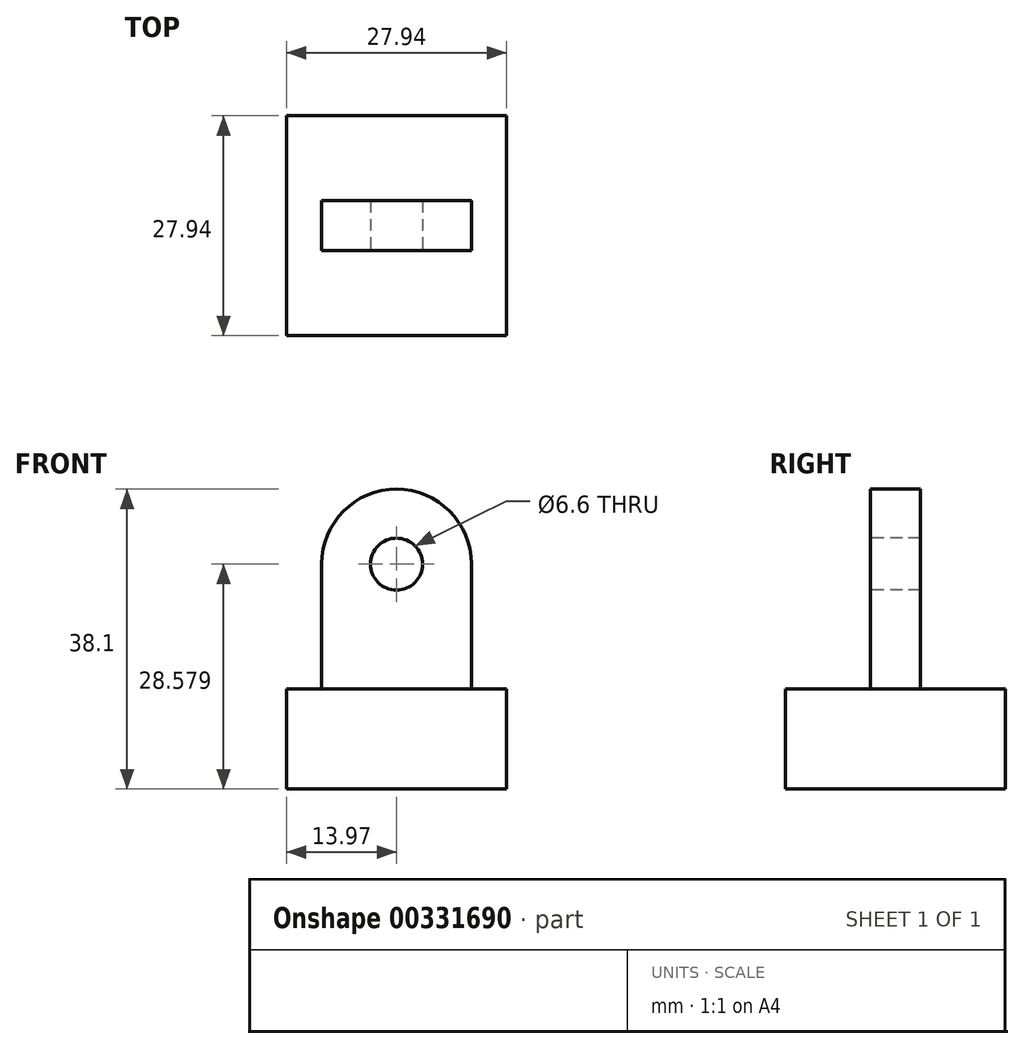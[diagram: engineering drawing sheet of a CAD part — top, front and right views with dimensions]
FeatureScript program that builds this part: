
annotation { "Feature Type Name" : "Feature", "Feature Type Description" : "" }
export const myFeature = defineFeature(function(context is Context, id is Id, definition is map)
    precondition{}
    {
        {
            var Q0;
            Q0=qCreatedBy(makeId("Front.planeOp"),FACE);
            var sketch = newSketch(context, id + "F0", { "sketchPlane" : qUnion([Q0])});
            skLineSegment(sketch, "E0.bottom", {"start": v(-27.94, -193.09) * mm, "end": v(0, -193.09) * mm});
            skLineSegment(sketch, "E0.top", {"start": v(-27.94, -205.79) * mm, "end": v(0, -205.79) * mm});
            skLineSegment(sketch, "E0.left", {"start": v(-27.94, -193.09) * mm, "end": v(-27.94, -205.79) * mm});
            skLineSegment(sketch, "E0.right", {"start": v(0, -193.09) * mm, "end": v(0, -205.79) * mm});
            skSolve(sketch);
        }
        {
            var Q0;
            Q0=makeQuery(id+"F0.imprint","IMPRINT",FACE,{"disambiguationData":[TD([[makeQuery(id+"F0.imprint","IMPRINT",EDGE,{"derivedFrom":sQuery(id+"F0.wireOp",EDGE,"E0.bottom")}),-1.0]])]});
            extrude(context, id + "F1", {"entities" : qUnion([Q0]), "oppositeDirection" : true, "depth" : 27.94 * mm});
        }
        {
            var Q0;
            Q0=makeQuery(id+"F1.opExtrude","SWEPT_FACE",FACE,{"disambiguationData":[OSD([sQuery(id+"F0.wireOp",EDGE,"E0.bottom")])]});
            var sketch = newSketch(context, id + "F2", { "sketchPlane" : qUnion([Q0])});
            skLineSegment(sketch, "E1.bottom", {"start": v(-23.5, 17.15) * mm, "end": v(-4.44, 17.15) * mm});
            skLineSegment(sketch, "E1.top", {"start": v(-23.5, 10.8) * mm, "end": v(-4.44, 10.8) * mm});
            skLineSegment(sketch, "E1.left", {"start": v(-23.5, 17.15) * mm, "end": v(-23.5, 10.8) * mm});
            skLineSegment(sketch, "E1.right", {"start": v(-4.44, 17.15) * mm, "end": v(-4.44, 10.8) * mm});
            skSolve(sketch);
        }
        {
            var Q0;
            Q0=makeQuery(id+"F2.imprint","IMPRINT",FACE,{"disambiguationData":[TD([[makeQuery(id+"F2.imprint","IMPRINT",EDGE,{"derivedFrom":sQuery(id+"F2.wireOp",EDGE,"E1.bottom")}),-1.0]])]});
            extrude(context, id + "F3", {"entities" : qUnion([Q0]), "operationType" : NewBodyOperationType.ADD, "depth" : 25.4 * mm});
        }
        {
            var Q0;
            Q0=makeQuery(id+"F3.opExtrude","CAP_EDGE",EDGE,{"disambiguationData":[OSD([sQuery(id+"F2.wireOp",EDGE,"E1.right")])],"isStart":false});
            var Q1;
            Q1=makeQuery(id+"F3.opExtrude","CAP_EDGE",EDGE,{"disambiguationData":[OSD([sQuery(id+"F2.wireOp",EDGE,"E1.left")])],"isStart":false});
            fillet(context, id + "F4", {"entities" : qUnion([Q0, Q1]), "radius" : 9.52 * mm, "tangentPropagation" : true, "allowEdgeOverflow" : false});
        }
        {
            var Q0;
            Q0=makeQuery(id+"F3.opExtrude","SWEPT_FACE",FACE,{"disambiguationData":[OSD([sQuery(id+"F2.wireOp",EDGE,"E1.top")])]});
            var sketch = newSketch(context, id + "F5", { "sketchPlane" : qUnion([Q0])});
            skCircle(sketch, "E2", {"center": v(-13.97, -177.21) * mm, "radius": 3.3 * mm});
            skSolve(sketch);
        }
        {
            var Q0;
            Q0=qSketchRegion(id+"F5",true);
            extrude(context, id + "F6", {"entities" : qUnion([Q0]), "operationType" : NewBodyOperationType.REMOVE, "oppositeDirection" : true, "depth" : 6.35 * mm});
        }
        {
            var Q0;
            Q0=makeQuery(id+"F1.opExtrude","SWEPT_FACE",FACE,{"disambiguationData":[OSD([sQuery(id+"F0.wireOp",EDGE,"E0.left")])]});
            var sketch = newSketch(context, id + "F7", { "sketchPlane" : qUnion([Q0])});
            skLineSegment(sketch, "E3.bottom", {"start": v(-26.35, -170.86) * mm, "end": v(-24.77, -170.86) * mm});
            skLineSegment(sketch, "E3.top", {"start": v(-26.35, -183.56) * mm, "end": v(-24.77, -183.56) * mm});
            skLineSegment(sketch, "E3.left", {"start": v(-26.35, -170.86) * mm, "end": v(-26.35, -183.56) * mm});
            skLineSegment(sketch, "E3.right", {"start": v(-24.77, -170.86) * mm, "end": v(-24.77, -183.56) * mm});
            skSolve(sketch);
        }
        {
            var Q0;
            Q0=qSketchRegion(id+"F7",true);
            extrude(context, id + "F8", {"entities" : qUnion([Q0]), "operationType" : NewBodyOperationType.REMOVE, "oppositeDirection" : true, "depth" : 22.22 * mm});
        }
    });
